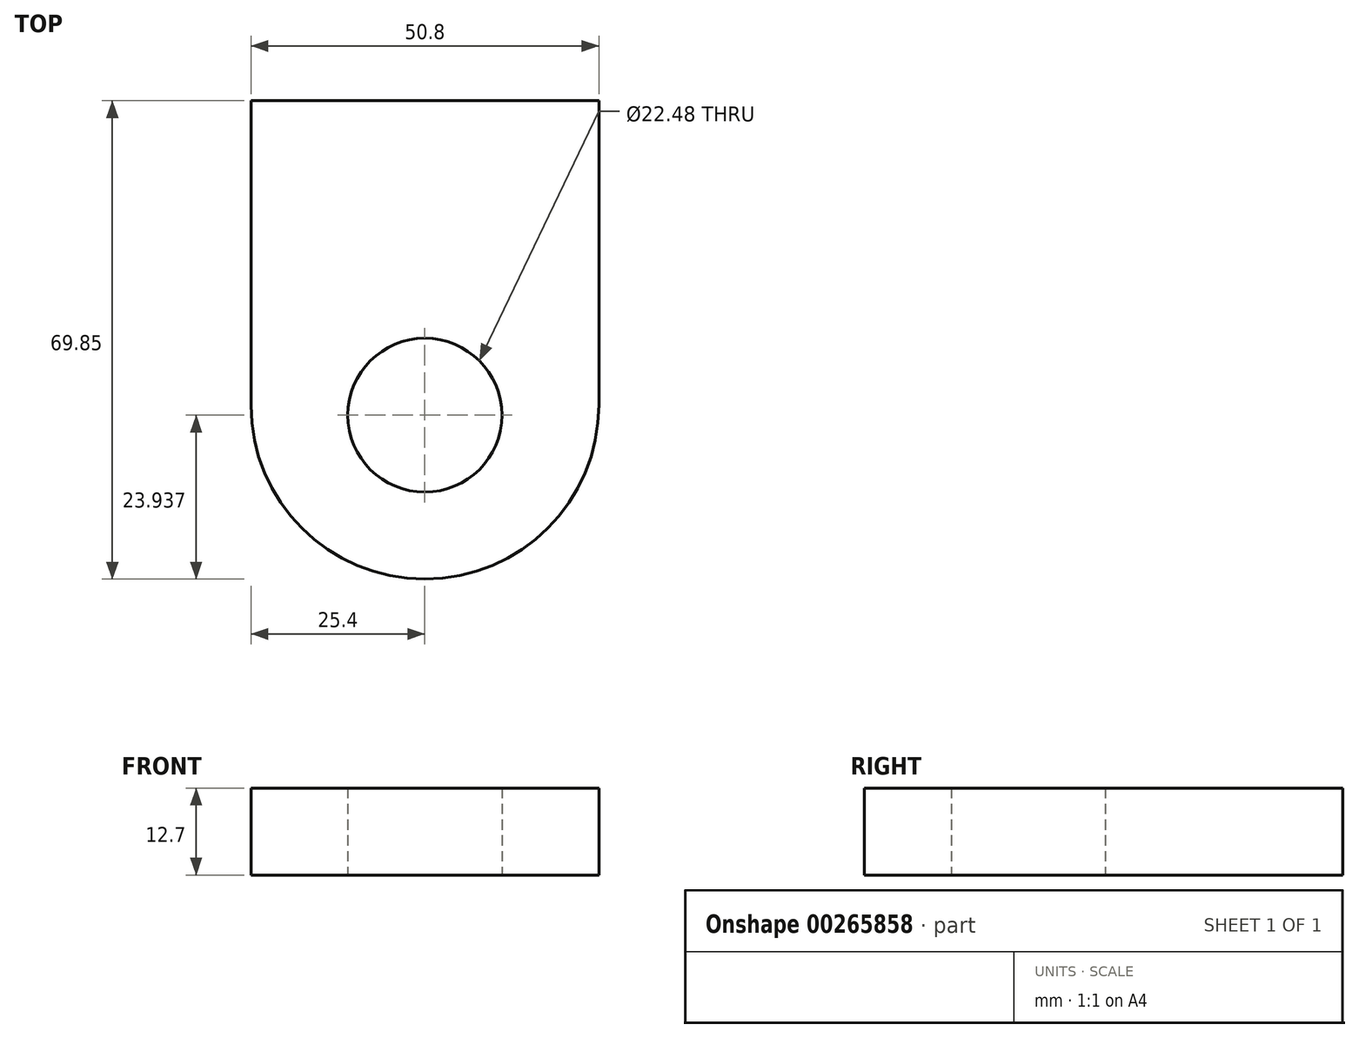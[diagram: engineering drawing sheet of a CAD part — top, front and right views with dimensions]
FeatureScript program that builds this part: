
annotation { "Feature Type Name" : "Feature", "Feature Type Description" : "" }
export const myFeature = defineFeature(function(context is Context, id is Id, definition is map)
    precondition{}
    {
        {
            var Q0;
            Q0=qCreatedBy(makeId("Top.planeOp"),FACE);
            var sketch = newSketch(context, id + "F0", { "sketchPlane" : qUnion([Q0])});
            skLineSegment(sketch, "E0.bottom", {"start": v(25.4, -22.23) * mm, "end": v(-25.4, -22.23) * mm});
            skLineSegment(sketch, "E0.top", {"start": v(25.4, 22.23) * mm, "end": v(-25.4, 22.23) * mm});
            skLineSegment(sketch, "E0.left", {"start": v(25.4, -22.23) * mm, "end": v(25.4, 22.23) * mm});
            skLineSegment(sketch, "E0.right", {"start": v(-25.4, -22.23) * mm, "end": v(-25.4, 22.23) * mm});
            skPoint(sketch, "E0.middle", {"position": v(0, 0) * mm});
            skArc(sketch, "E1", {"start": v(-25.4, -22.23) * mm, "mid": v(0, -47.63) * mm, "end": v(25.4, -22.23) * mm});
            skSolve(sketch);
        }
        {
            var Q0;
            Q0 = qSketchRegion(id + "F0", true);
            extrude(context, id + "F1", {"entities" : qUnion([Q0]), "depth" : 12.7 * mm});
        }
        {
            var Q0;
            Q0=qCreatedBy(makeId("Top.planeOp"),FACE);
            var sketch = newSketch(context, id + "F2", { "sketchPlane" : qUnion([Q0])});
            skCircle(sketch, "E2", {"center": v(0, -23.68) * mm, "radius": 11.24 * mm});
            skSolve(sketch);
        }
        {
            var Q0;
            Q0 = qSketchRegion(id + "F2", true);
            extrude(context, id + "F3", {"entities" : qUnion([Q0]), "operationType" : NewBodyOperationType.REMOVE, "depth" : 12.7 * mm});
        }
    });
